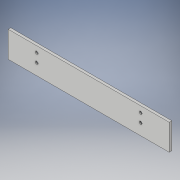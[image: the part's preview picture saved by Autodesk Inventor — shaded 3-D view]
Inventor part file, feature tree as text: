
AUTODESK INVENTOR PART (.ipt)
format: ipt  version: 2019 (Build 230136000, 136)  size: 113,152 bytes
history: native  units: in
note: dims shown in document units (in); Inventor stores cm internally (conversion verified against a paired STEP export)
features: sketch x2, extrude x1, hole x1
ambient origin geometry x8: Origin, YZ Plane, XZ Plane, XY Plane, X Axis, Y Axis, Z Axis, Center Point
bodies: Solid1 (feature_tree)
feature tree (4):
  extrude  "Extrusion1"  Depth=1.1811in
  hole  "Hole1"  [1 undecoded]
  sketch  "Sketch1"  dims[d0=7.3228in d1=1.1811in]
  sketch  "Sketch2"  dims[d2=0.1181in d3=0.0in d16=1.2992in d17=0.5118in d18=1.299in d19=0.2756in d20=1.2992in d21=0.1339in d22=0.7087in d23=0.2717in d24=0.0394in d25=0.6181in d26=0.7087in d27=0.8108in]
note: 1 required parameter value undecoded (feature->parameter linkage not recoverable at this tier; creation-order binding heuristic only, values carry confidence <= 0.55)
